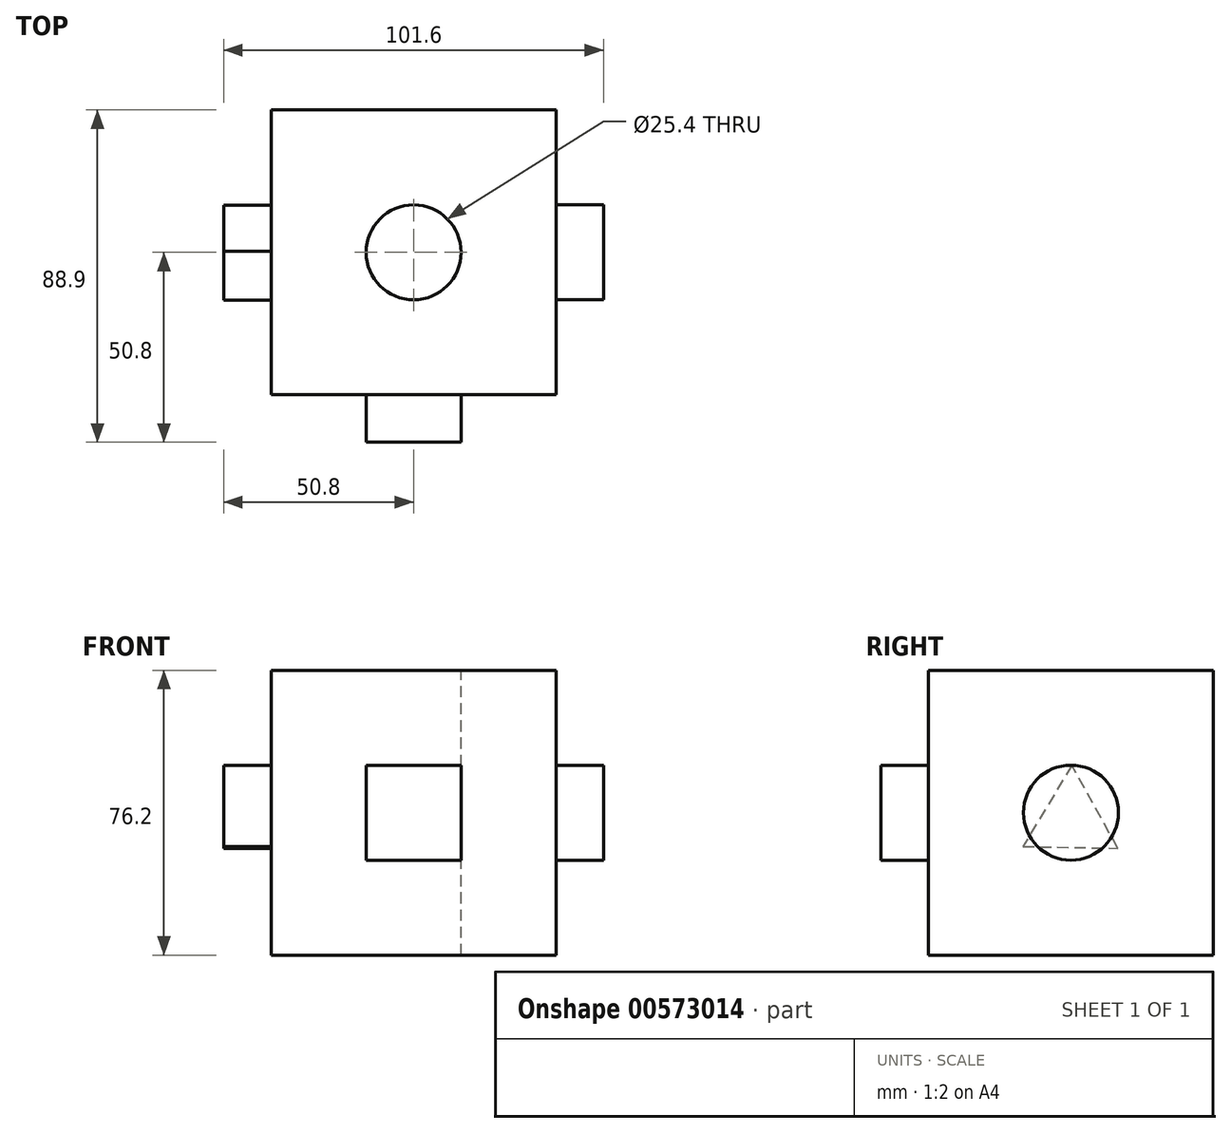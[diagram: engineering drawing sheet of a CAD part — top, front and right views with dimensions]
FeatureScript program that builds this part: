
annotation { "Feature Type Name" : "Feature", "Feature Type Description" : "" }
export const myFeature = defineFeature(function(context is Context, id is Id, definition is map)
    precondition{}
    {
        {
            var Q0;
            Q0=qCreatedBy(makeId("Front.planeOp"),FACE);
            var sketch = newSketch(context, id + "F0", { "sketchPlane" : qUnion([Q0])});
            skLineSegment(sketch, "E0.bottom", {"start": v(-30.8, -26.43) * mm, "end": v(45.4, -26.43) * mm});
            skLineSegment(sketch, "E0.top", {"start": v(-30.8, 49.77) * mm, "end": v(45.4, 49.77) * mm});
            skLineSegment(sketch, "E0.left", {"start": v(-30.8, -26.43) * mm, "end": v(-30.8, 49.77) * mm});
            skLineSegment(sketch, "E0.right", {"start": v(45.4, -26.43) * mm, "end": v(45.4, 49.77) * mm});
            skSolve(sketch);
        }
        {
            var Q0;
            Q0 = qSketchRegion(id + "F0", true);
            extrude(context, id + "F1", {"entities" : qUnion([Q0]), "oppositeDirection" : true, "depth" : 76.2 * mm, "offsetDistance" : 25.4 * mm});
        }
        {
            var Q0;
            Q0=makeQuery(id+"F1.opExtrude","CAP_FACE",FACE,{"disambiguationData":[OSD([sQuery(id+"F0.wireOp",EDGE,"E0.bottom"),sQuery(id+"F0.wireOp",EDGE,"E0.top"),sQuery(id+"F0.wireOp",EDGE,"E0.left"),sQuery(id+"F0.wireOp",EDGE,"E0.right")])],"isStart":true});
            var sketch = newSketch(context, id + "F2", { "sketchPlane" : qUnion([Q0])});
            skLineSegment(sketch, "E1.bottom", {"start": v(-5.4, -1.03) * mm, "end": v(20, -1.03) * mm});
            skLineSegment(sketch, "E1.top", {"start": v(-5.4, 24.37) * mm, "end": v(20, 24.37) * mm});
            skLineSegment(sketch, "E1.left", {"start": v(-5.4, -1.03) * mm, "end": v(-5.4, 24.37) * mm});
            skLineSegment(sketch, "E1.right", {"start": v(20, -1.03) * mm, "end": v(20, 24.37) * mm});
            skSolve(sketch);
        }
        {
            var Q0;
            Q0=makeQuery(id+"F2.imprint","IMPRINT",FACE,{"disambiguationData":[TD([[makeQuery(id+"F2.imprint","IMPRINT",EDGE,{"derivedFrom":sQuery(id+"F2.wireOp",EDGE,"E1.bottom")}),1.0]])]});
            extrude(context, id + "F3", {"entities" : qUnion([Q0]), "operationType" : NewBodyOperationType.ADD, "depth" : 12.7 * mm, "offsetDistance" : 25.4 * mm});
        }
        {
            var Q0;
            Q0=makeQuery(id+"F1.opExtrude","SWEPT_FACE",FACE,{"disambiguationData":[OSD([sQuery(id+"F0.wireOp",EDGE,"E0.right")])]});
            var sketch = newSketch(context, id + "F4", { "sketchPlane" : qUnion([Q0])});
            skCircle(sketch, "E2", {"center": v(38.1, 11.67) * mm, "radius": 12.7 * mm});
            skSolve(sketch);
        }
        {
            var Q0;
            Q0=makeQuery(id+"F4.imprint","IMPRINT",FACE,{"disambiguationData":[TD([[makeQuery(id+"F4.imprint","IMPRINT",EDGE,{"derivedFrom":sQuery(id+"F4.wireOp",EDGE,"E2")}),1.0]])]});
            extrude(context, id + "F5", {"entities" : qUnion([Q0]), "operationType" : NewBodyOperationType.ADD, "depth" : 12.7 * mm, "offsetDistance" : 25.4 * mm});
        }
        {
            var Q0;
            Q0=makeQuery(id+"F1.opExtrude","SWEPT_FACE",FACE,{"disambiguationData":[OSD([sQuery(id+"F0.wireOp",EDGE,"E0.top")])]});
            var sketch = newSketch(context, id + "F6", { "sketchPlane" : qUnion([Q0])});
            skPoint(sketch, "E3", {"position": v(7.3, 38.1) * mm});
            skSolve(sketch);
        }
        {
            var Q0;
            Q0=sQuery(id+"F6.wireOp",VERTEX,"E3");
            var Q1;
            Q1=makeQuery(id+"F1.opExtrude","SWEPT_BODY",BODY,{"disambiguationData":[OSD([sQuery(id+"F0.wireOp",EDGE,"E0.bottom"),sQuery(id+"F0.wireOp",EDGE,"E0.top"),sQuery(id+"F0.wireOp",EDGE,"E0.left"),sQuery(id+"F0.wireOp",EDGE,"E0.right")])]});
            hole(context, id + "F7", {"style" : HoleStyle.SIMPLE, "endStyle" : HoleEndStyle.THROUGH, "holeDiameter" : 25.4 * mm, "isTappedThrough" : true, "tappedDepth" : 12.7 * mm, "tapClearance" : 3, "locations" : qUnion([Q0]), "scope" : qUnion([Q1])});
        }
        {
            var Q0;
            Q0=makeQuery(id+"F1.opExtrude","SWEPT_FACE",FACE,{"disambiguationData":[OSD([sQuery(id+"F0.wireOp",EDGE,"E0.left")])]});
            var sketch = newSketch(context, id + "F8", { "sketchPlane" : qUnion([Q0])});
            skCircle(sketch, "E4.cCircle", {"center": v(-38.1, 9.71) * mm, "radius": 7.33 * mm, "construction": true});
            skLineSegment(sketch, "E4.0", {"start": v(-38.36, 24.37) * mm, "end": v(-25.27, 2.6) * mm});
            skLineSegment(sketch, "E4.1", {"start": v(-25.27, 2.6) * mm, "end": v(-50.67, 2.16) * mm});
            skLineSegment(sketch, "E4.2", {"start": v(-50.67, 2.16) * mm, "end": v(-38.36, 24.37) * mm});
            skPoint(sketch, "E4.0.midPoint", {"position": v(-31.81, 13.49) * mm});
            skSolve(sketch);
        }
        {
            var Q0;
            Q0=makeQuery(id+"F8.imprint","IMPRINT",FACE,{"disambiguationData":[TD([[makeQuery(id+"F8.imprint","IMPRINT",EDGE,{"derivedFrom":sQuery(id+"F8.wireOp",EDGE,"E4.0")}),-1.0]])]});
            extrude(context, id + "F9", {"entities" : qUnion([Q0]), "operationType" : NewBodyOperationType.ADD, "depth" : 12.7 * mm, "offsetDistance" : 25.4 * mm});
        }
    });
